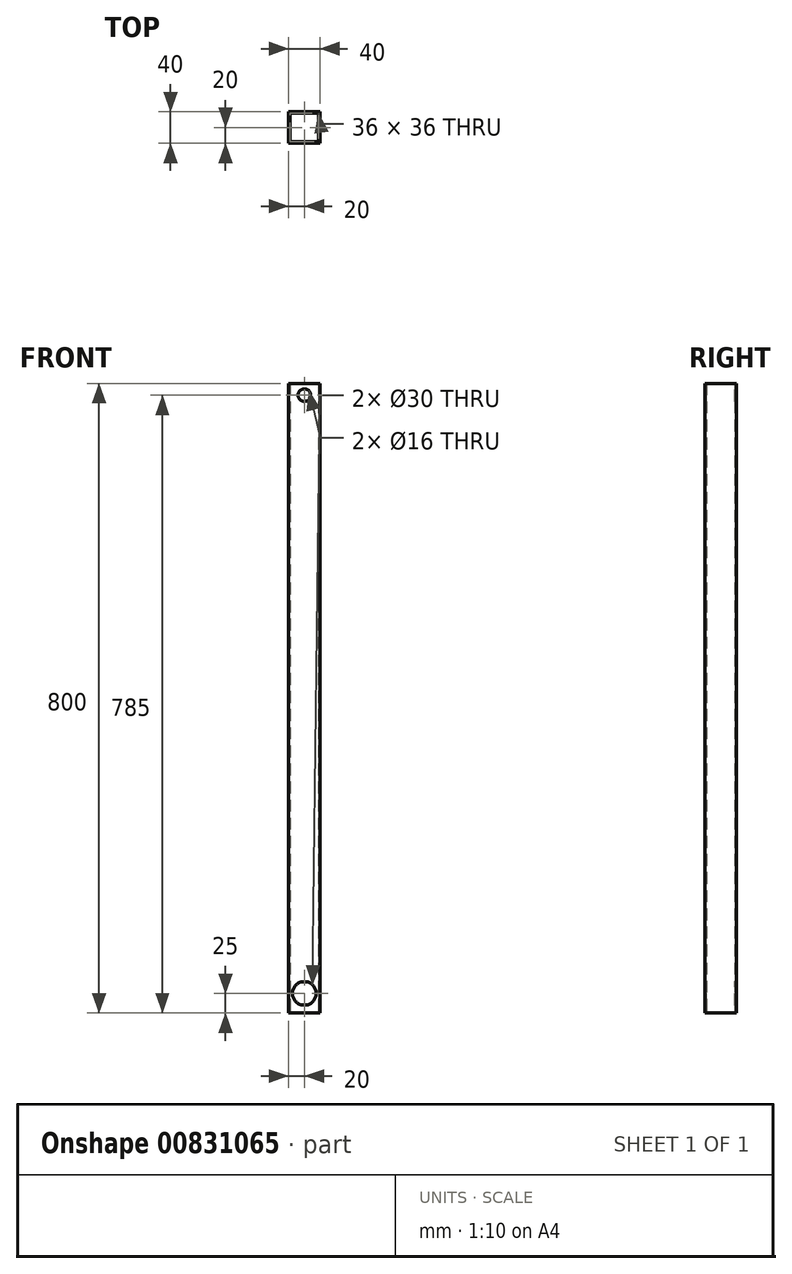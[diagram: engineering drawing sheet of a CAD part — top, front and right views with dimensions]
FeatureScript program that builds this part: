
annotation { "Feature Type Name" : "Feature", "Feature Type Description" : "" }
export const myFeature = defineFeature(function(context is Context, id is Id, definition is map)
    precondition{}
    {
        {
            var Q0;
            Q0=qCreatedBy(makeId("Top.planeOp"),FACE);
            var sketch = newSketch(context, id + "F0", { "sketchPlane" : qUnion([Q0])});
            skLineSegment(sketch, "E0.bottom", {"start": v(20, 20) * mm, "end": v(-20, 20) * mm});
            skLineSegment(sketch, "E0.top", {"start": v(20, -20) * mm, "end": v(-20, -20) * mm});
            skLineSegment(sketch, "E0.left", {"start": v(20, 20) * mm, "end": v(20, -20) * mm});
            skLineSegment(sketch, "E0.right", {"start": v(-20, 20) * mm, "end": v(-20, -20) * mm});
            skPoint(sketch, "E0.middle", {"position": v(0, 0) * mm});
            skLineSegment(sketch, "E1.bottom", {"start": v(18, 18) * mm, "end": v(-18, 18) * mm});
            skLineSegment(sketch, "E1.top", {"start": v(18, -18) * mm, "end": v(-18, -18) * mm});
            skLineSegment(sketch, "E1.left", {"start": v(18, 18) * mm, "end": v(18, -18) * mm});
            skLineSegment(sketch, "E1.right", {"start": v(-18, 18) * mm, "end": v(-18, -18) * mm});
            skSolve(sketch);
        }
        {
            var Q0;
            Q0=makeQuery(id+"F0.imprint","IMPRINT",FACE,{"disambiguationData":[TD([[makeQuery(id+"F0.imprint","IMPRINT",EDGE,{"derivedFrom":sQuery(id+"F0.wireOp",EDGE,"E0.bottom")}),1.0]])]});
            extrude(context, id + "F1", {"entities" : qUnion([Q0]), "depth" : 800 * mm, "offsetDistance" : 25 * mm});
        }
        {
            var Q0;
            Q0=makeQuery(id+"F1.opExtrude","SWEPT_FACE",FACE,{"disambiguationData":[OSD([sQuery(id+"F0.wireOp",EDGE,"E0.bottom")])]});
            var sketch = newSketch(context, id + "F2", { "sketchPlane" : qUnion([Q0])});
            skCircle(sketch, "E2", {"center": v(0, 785) * mm, "radius": 8 * mm});
            skPoint(sketch, "E2.centerSnap0", {"position": v(0, 800) * mm});
            skCircle(sketch, "E3", {"center": v(0, 25) * mm, "radius": 15 * mm});
            skSolve(sketch);
        }
        {
            var Q0;
            Q0=makeQuery(id+"F2.imprint","IMPRINT",FACE,{"disambiguationData":[TD([[makeQuery(id+"F2.imprint","IMPRINT",EDGE,{"derivedFrom":sQuery(id+"F2.wireOp",EDGE,"E2")}),1.0]])]});
            var Q1;
            Q1=makeQuery(id+"F2.imprint","IMPRINT",FACE,{"disambiguationData":[TD([[makeQuery(id+"F2.imprint","IMPRINT",EDGE,{"derivedFrom":sQuery(id+"F2.wireOp",EDGE,"E3")}),1.0]])]});
            extrude(context, id + "F3", {"entities" : qUnion([Q0, Q1]), "operationType" : NewBodyOperationType.REMOVE, "endBound" : BoundingType.THROUGH_ALL, "oppositeDirection" : true, "depth" : 25 * mm, "offsetDistance" : 25 * mm});
        }
    });
